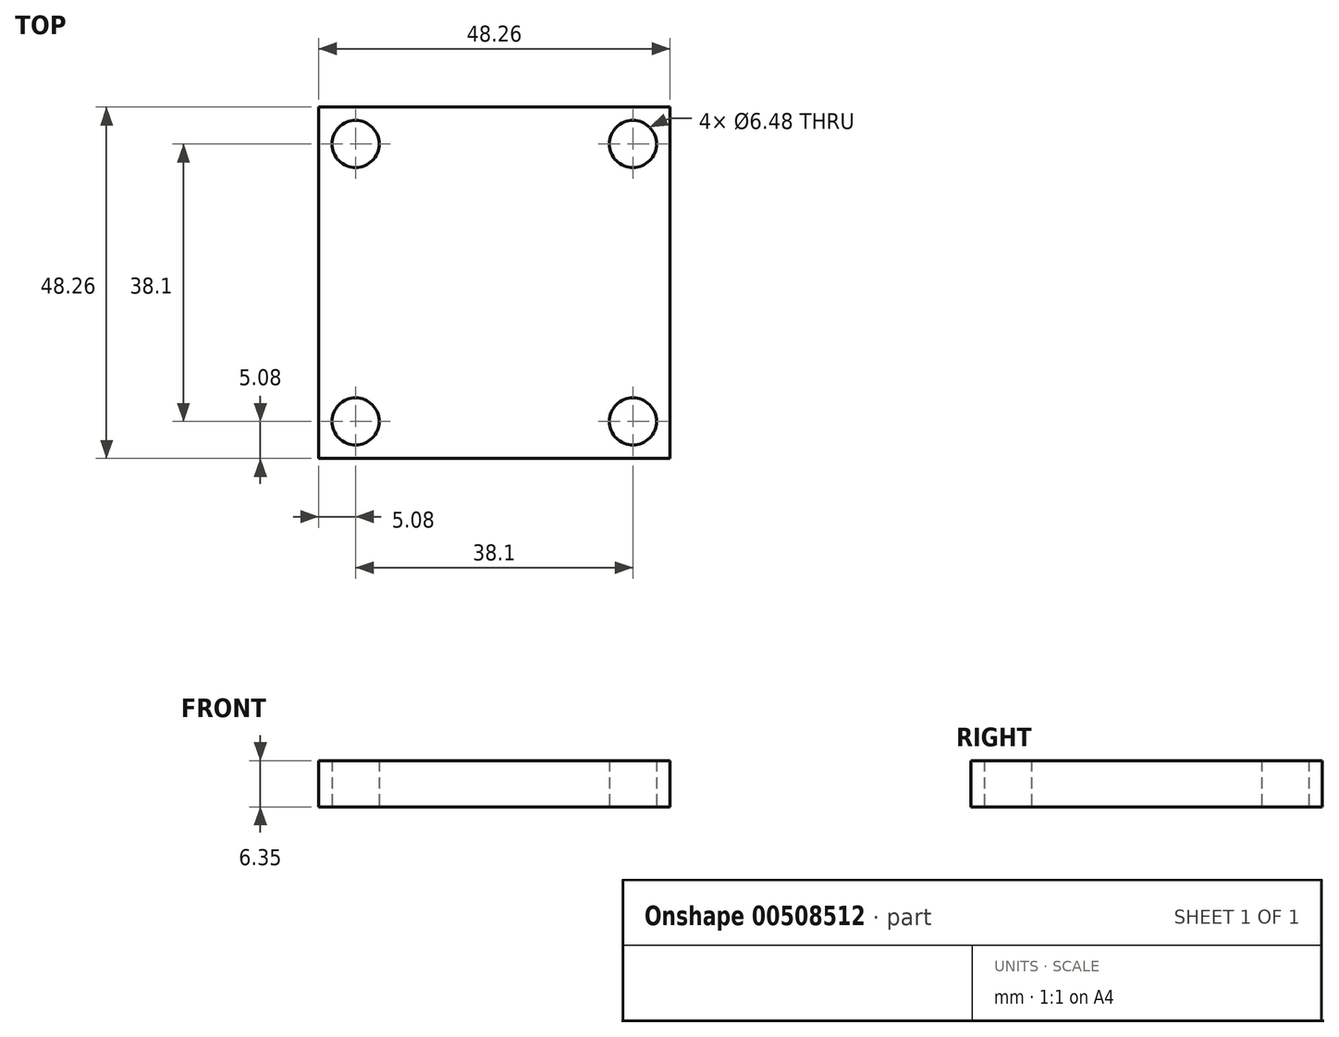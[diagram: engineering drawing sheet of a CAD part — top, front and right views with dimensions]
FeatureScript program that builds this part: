
annotation { "Feature Type Name" : "Feature", "Feature Type Description" : "" }
export const myFeature = defineFeature(function(context is Context, id is Id, definition is map)
    precondition{}
    {
        {
            var Q0;
            Q0=qCreatedBy(makeId("Top.planeOp"),FACE);
            var sketch = newSketch(context, id + "F0", { "sketchPlane" : qUnion([Q0])});
            skLineSegment(sketch, "E0.bottom", {"start": v(0, 0) * mm, "end": v(48.26, 0) * mm});
            skLineSegment(sketch, "E0.top", {"start": v(0, -48.26) * mm, "end": v(48.26, -48.26) * mm});
            skLineSegment(sketch, "E0.left", {"start": v(0, 0) * mm, "end": v(0, -48.26) * mm});
            skLineSegment(sketch, "E0.right", {"start": v(48.26, 0) * mm, "end": v(48.26, -48.26) * mm});
            skLineSegment(sketch, "E1.bottom", {"start": v(5.08, -5.08) * mm, "end": v(43.18, -5.08) * mm, "construction": true});
            skLineSegment(sketch, "E1.top", {"start": v(5.08, -43.18) * mm, "end": v(43.18, -43.18) * mm, "construction": true});
            skLineSegment(sketch, "E1.left", {"start": v(5.08, -5.08) * mm, "end": v(5.08, -43.18) * mm, "construction": true});
            skLineSegment(sketch, "E1.right", {"start": v(43.18, -5.08) * mm, "end": v(43.18, -43.18) * mm, "construction": true});
            skPoint(sketch, "E2", {"position": v(24.13, -24.13) * mm});
            skCircle(sketch, "E3", {"center": v(43.18, -5.08) * mm, "radius": 3.24 * mm});
            skCircle(sketch, "E4", {"center": v(5.08, -5.08) * mm, "radius": 3.24 * mm});
            skCircle(sketch, "E5", {"center": v(5.08, -43.18) * mm, "radius": 3.24 * mm});
            skCircle(sketch, "E6", {"center": v(43.18, -43.18) * mm, "radius": 3.24 * mm});
            skSolve(sketch);
        }
        {
            var Q0;
            Q0=makeQuery(id+"F0.imprint","IMPRINT",FACE,{"disambiguationData":[TD([[makeQuery(id+"F0.imprint","IMPRINT",EDGE,{"derivedFrom":sQuery(id+"F0.wireOp",EDGE,"E0.bottom")}),-1.0]])]});
            extrude(context, id + "F1", {"entities" : qUnion([Q0]), "depth" : 6.35 * mm, "offsetDistance" : 25.4 * mm});
        }
    });
